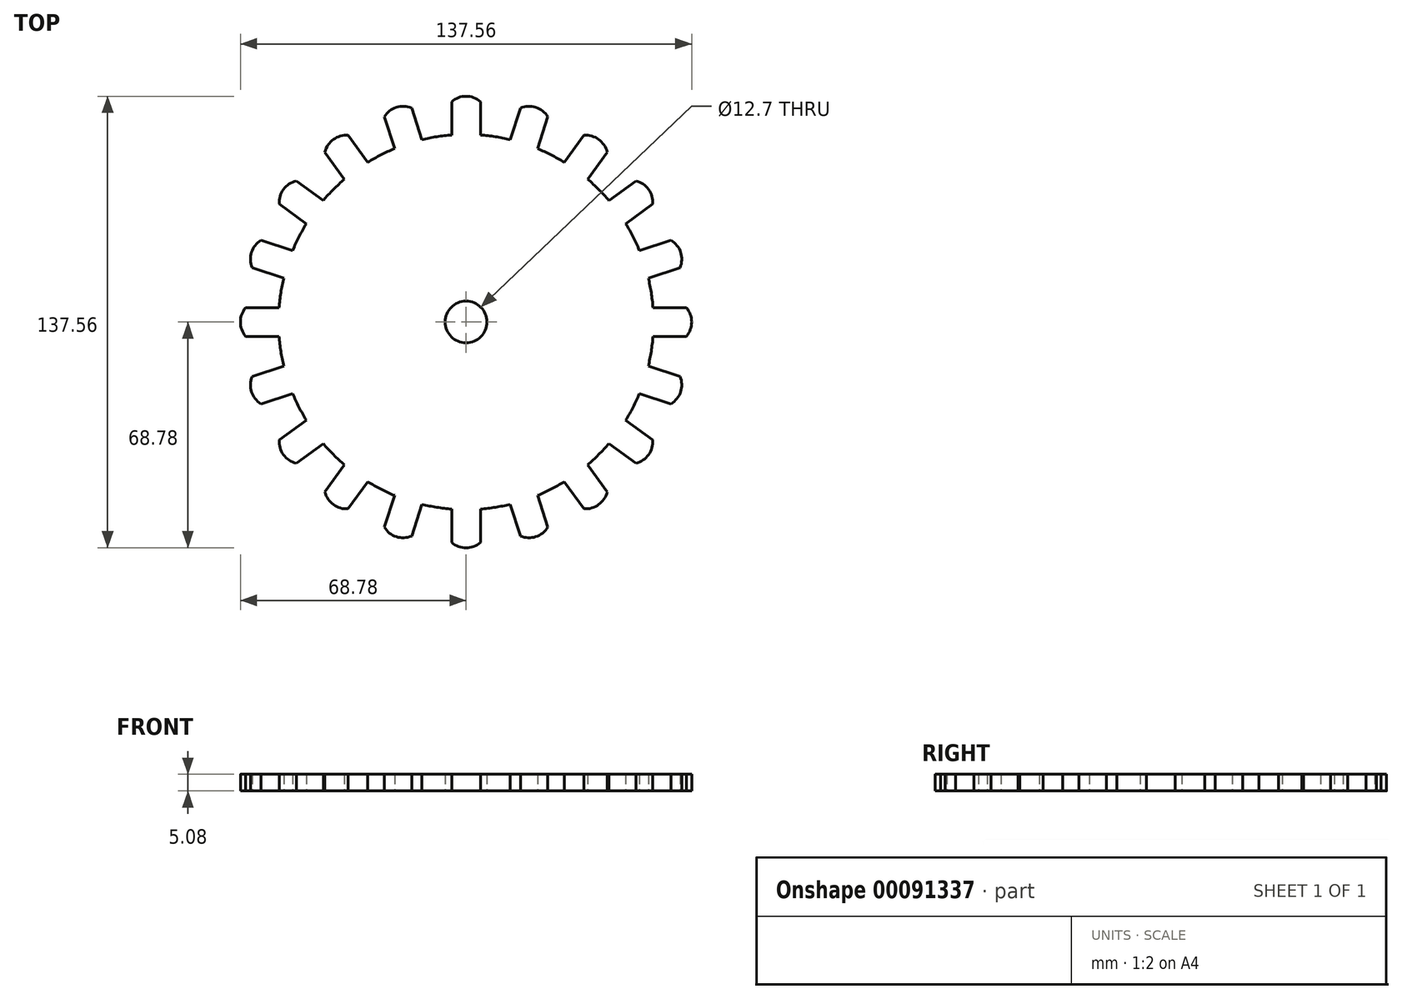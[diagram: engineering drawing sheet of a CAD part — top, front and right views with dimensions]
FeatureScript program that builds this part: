
annotation { "Feature Type Name" : "Feature", "Feature Type Description" : "" }
export const myFeature = defineFeature(function(context is Context, id is Id, definition is map)
    precondition{}
    {
        {
            var Q0;
            Q0=qCreatedBy(makeId("Top.planeOp"),FACE);
            var sketch = newSketch(context, id + "F0", { "sketchPlane" : qUnion([Q0])});
            skArc(sketch, "E0", {"start": v(-4.4, 56.98) * mm, "mid": v(-8.94, 56.45) * mm, "end": v(-13.43, 55.55) * mm});
            skLineSegment(sketch, "E1.left", {"start": v(4.4, 56.98) * mm, "end": v(4.4, 67.14) * mm});
            skLineSegment(sketch, "E1.right", {"start": v(-4.4, 56.98) * mm, "end": v(-4.4, 67.14) * mm});
            skArc(sketch, "E2", {"start": v(4.4, 67.14) * mm, "mid": v(0, 68.78) * mm, "end": v(-4.4, 67.14) * mm});
            skPoint(sketch, "E3.start.orphan", {"position": v(0, 67.14) * mm});
            skLineSegment(sketch, "E4.1.0", {"start": v(-13.43, 55.55) * mm, "end": v(-16.57, 65.21) * mm});
            skArc(sketch, "E4.1.1", {"start": v(-16.57, 65.21) * mm, "mid": v(-21.25, 65.41) * mm, "end": v(-24.92, 62.5) * mm});
            skLineSegment(sketch, "E4.1.2", {"start": v(-21.79, 52.83) * mm, "end": v(-24.92, 62.5) * mm});
            skLineSegment(sketch, "E4.2.0", {"start": v(-29.94, 48.68) * mm, "end": v(-35.91, 56.9) * mm});
            skArc(sketch, "E4.2.1", {"start": v(-35.91, 56.9) * mm, "mid": v(-40.43, 55.64) * mm, "end": v(-43.02, 51.74) * mm});
            skLineSegment(sketch, "E4.2.2", {"start": v(-37.05, 43.52) * mm, "end": v(-43.02, 51.74) * mm});
            skLineSegment(sketch, "E4.3.0", {"start": v(-43.52, 37.05) * mm, "end": v(-51.74, 43.02) * mm});
            skArc(sketch, "E4.3.1", {"start": v(-51.74, 43.02) * mm, "mid": v(-55.64, 40.43) * mm, "end": v(-56.9, 35.91) * mm});
            skLineSegment(sketch, "E4.3.2", {"start": v(-48.68, 29.94) * mm, "end": v(-56.9, 35.91) * mm});
            skLineSegment(sketch, "E4.4.0", {"start": v(-52.83, 21.79) * mm, "end": v(-62.5, 24.92) * mm});
            skArc(sketch, "E4.4.1", {"start": v(-62.5, 24.92) * mm, "mid": v(-65.41, 21.25) * mm, "end": v(-65.21, 16.57) * mm});
            skLineSegment(sketch, "E4.4.2", {"start": v(-55.55, 13.43) * mm, "end": v(-65.21, 16.57) * mm});
            skLineSegment(sketch, "E4.5.0", {"start": v(-56.98, 4.4) * mm, "end": v(-67.14, 4.4) * mm});
            skArc(sketch, "E4.5.1", {"start": v(-67.14, 4.4) * mm, "mid": v(-68.78, 0) * mm, "end": v(-67.14, -4.4) * mm});
            skLineSegment(sketch, "E4.5.2", {"start": v(-56.98, -4.4) * mm, "end": v(-67.14, -4.4) * mm});
            skLineSegment(sketch, "E4.6.0", {"start": v(-55.55, -13.43) * mm, "end": v(-65.21, -16.57) * mm});
            skArc(sketch, "E4.6.1", {"start": v(-65.21, -16.57) * mm, "mid": v(-65.41, -21.25) * mm, "end": v(-62.5, -24.92) * mm});
            skLineSegment(sketch, "E4.6.2", {"start": v(-52.83, -21.79) * mm, "end": v(-62.5, -24.92) * mm});
            skLineSegment(sketch, "E4.7.0", {"start": v(-48.68, -29.94) * mm, "end": v(-56.9, -35.91) * mm});
            skArc(sketch, "E4.7.1", {"start": v(-56.9, -35.91) * mm, "mid": v(-55.64, -40.43) * mm, "end": v(-51.74, -43.02) * mm});
            skLineSegment(sketch, "E4.7.2", {"start": v(-43.52, -37.05) * mm, "end": v(-51.74, -43.02) * mm});
            skLineSegment(sketch, "E4.8.0", {"start": v(-37.05, -43.52) * mm, "end": v(-43.02, -51.74) * mm});
            skArc(sketch, "E4.8.1", {"start": v(-43.02, -51.74) * mm, "mid": v(-40.43, -55.64) * mm, "end": v(-35.91, -56.9) * mm});
            skLineSegment(sketch, "E4.8.2", {"start": v(-29.94, -48.68) * mm, "end": v(-35.91, -56.9) * mm});
            skLineSegment(sketch, "E4.9.0", {"start": v(-21.79, -52.83) * mm, "end": v(-24.92, -62.5) * mm});
            skArc(sketch, "E4.9.1", {"start": v(-24.92, -62.5) * mm, "mid": v(-21.25, -65.41) * mm, "end": v(-16.57, -65.21) * mm});
            skLineSegment(sketch, "E4.9.2", {"start": v(-13.43, -55.55) * mm, "end": v(-16.57, -65.21) * mm});
            skLineSegment(sketch, "E4.10.0", {"start": v(-4.4, -56.98) * mm, "end": v(-4.4, -67.14) * mm});
            skArc(sketch, "E4.10.1", {"start": v(-4.4, -67.14) * mm, "mid": v(0, -68.78) * mm, "end": v(4.4, -67.14) * mm});
            skLineSegment(sketch, "E4.10.2", {"start": v(4.4, -56.98) * mm, "end": v(4.4, -67.14) * mm});
            skLineSegment(sketch, "E4.11.0", {"start": v(13.43, -55.55) * mm, "end": v(16.57, -65.21) * mm});
            skArc(sketch, "E4.11.1", {"start": v(16.57, -65.21) * mm, "mid": v(21.25, -65.41) * mm, "end": v(24.92, -62.5) * mm});
            skLineSegment(sketch, "E4.11.2", {"start": v(21.79, -52.83) * mm, "end": v(24.92, -62.5) * mm});
            skLineSegment(sketch, "E4.12.0", {"start": v(29.94, -48.68) * mm, "end": v(35.91, -56.9) * mm});
            skArc(sketch, "E4.12.1", {"start": v(35.91, -56.9) * mm, "mid": v(40.43, -55.64) * mm, "end": v(43.02, -51.74) * mm});
            skLineSegment(sketch, "E4.12.2", {"start": v(37.05, -43.52) * mm, "end": v(43.02, -51.74) * mm});
            skLineSegment(sketch, "E4.13.0", {"start": v(43.52, -37.05) * mm, "end": v(51.74, -43.02) * mm});
            skArc(sketch, "E4.13.1", {"start": v(51.74, -43.02) * mm, "mid": v(55.64, -40.43) * mm, "end": v(56.9, -35.91) * mm});
            skLineSegment(sketch, "E4.13.2", {"start": v(48.68, -29.94) * mm, "end": v(56.9, -35.91) * mm});
            skLineSegment(sketch, "E4.14.0", {"start": v(52.83, -21.79) * mm, "end": v(62.5, -24.92) * mm});
            skArc(sketch, "E4.14.1", {"start": v(62.5, -24.92) * mm, "mid": v(65.41, -21.25) * mm, "end": v(65.21, -16.57) * mm});
            skLineSegment(sketch, "E4.14.2", {"start": v(55.55, -13.43) * mm, "end": v(65.21, -16.57) * mm});
            skLineSegment(sketch, "E4.15.0", {"start": v(56.98, -4.4) * mm, "end": v(67.14, -4.4) * mm});
            skArc(sketch, "E4.15.1", {"start": v(67.14, -4.4) * mm, "mid": v(68.78, 0) * mm, "end": v(67.14, 4.4) * mm});
            skLineSegment(sketch, "E4.15.2", {"start": v(56.98, 4.4) * mm, "end": v(67.14, 4.4) * mm});
            skLineSegment(sketch, "E4.16.0", {"start": v(55.55, 13.43) * mm, "end": v(65.21, 16.57) * mm});
            skArc(sketch, "E4.16.1", {"start": v(65.21, 16.57) * mm, "mid": v(65.41, 21.25) * mm, "end": v(62.5, 24.92) * mm});
            skLineSegment(sketch, "E4.16.2", {"start": v(52.83, 21.79) * mm, "end": v(62.5, 24.92) * mm});
            skLineSegment(sketch, "E4.17.0", {"start": v(48.68, 29.94) * mm, "end": v(56.9, 35.91) * mm});
            skArc(sketch, "E4.17.1", {"start": v(56.9, 35.91) * mm, "mid": v(55.64, 40.43) * mm, "end": v(51.74, 43.02) * mm});
            skLineSegment(sketch, "E4.17.2", {"start": v(43.52, 37.05) * mm, "end": v(51.74, 43.02) * mm});
            skLineSegment(sketch, "E4.18.0", {"start": v(37.05, 43.52) * mm, "end": v(43.02, 51.74) * mm});
            skArc(sketch, "E4.18.1", {"start": v(43.02, 51.74) * mm, "mid": v(40.43, 55.64) * mm, "end": v(35.91, 56.9) * mm});
            skLineSegment(sketch, "E4.18.2", {"start": v(29.94, 48.68) * mm, "end": v(35.91, 56.9) * mm});
            skLineSegment(sketch, "E4.19.0", {"start": v(21.79, 52.83) * mm, "end": v(24.92, 62.5) * mm});
            skArc(sketch, "E4.19.1", {"start": v(24.92, 62.5) * mm, "mid": v(21.25, 65.41) * mm, "end": v(16.57, 65.21) * mm});
            skLineSegment(sketch, "E4.19.2", {"start": v(13.43, 55.55) * mm, "end": v(16.57, 65.21) * mm});
            skArc(sketch, "E5.trimOffspring", {"start": v(-21.79, 52.83) * mm, "mid": v(-25.95, 50.92) * mm, "end": v(-29.94, 48.68) * mm});
            skArc(sketch, "E6.trimOffspring", {"start": v(-37.05, 43.52) * mm, "mid": v(-40.41, 40.41) * mm, "end": v(-43.52, 37.05) * mm});
            skArc(sketch, "E7.trimOffspring", {"start": v(-48.68, 29.94) * mm, "mid": v(-50.92, 25.95) * mm, "end": v(-52.83, 21.79) * mm});
            skArc(sketch, "E8.trimOffspring", {"start": v(-55.55, 13.43) * mm, "mid": v(-56.45, 8.94) * mm, "end": v(-56.98, 4.4) * mm});
            skArc(sketch, "E9.trimOffspring", {"start": v(-56.98, -4.4) * mm, "mid": v(-56.45, -8.94) * mm, "end": v(-55.55, -13.43) * mm});
            skArc(sketch, "E10.trimOffspring", {"start": v(-52.83, -21.79) * mm, "mid": v(-50.92, -25.95) * mm, "end": v(-48.68, -29.94) * mm});
            skArc(sketch, "E11.trimOffspring", {"start": v(-43.52, -37.05) * mm, "mid": v(-40.41, -40.41) * mm, "end": v(-37.05, -43.52) * mm});
            skArc(sketch, "E12.trimOffspring", {"start": v(-29.94, -48.68) * mm, "mid": v(-25.95, -50.92) * mm, "end": v(-21.79, -52.83) * mm});
            skArc(sketch, "E13.trimOffspring", {"start": v(-13.43, -55.55) * mm, "mid": v(-8.94, -56.45) * mm, "end": v(-4.4, -56.98) * mm});
            skArc(sketch, "E14.trimOffspring", {"start": v(4.4, -56.98) * mm, "mid": v(8.94, -56.45) * mm, "end": v(13.43, -55.55) * mm});
            skArc(sketch, "E15.trimOffspring", {"start": v(21.79, -52.83) * mm, "mid": v(25.95, -50.92) * mm, "end": v(29.94, -48.68) * mm});
            skArc(sketch, "E16.trimOffspring", {"start": v(37.05, -43.52) * mm, "mid": v(40.41, -40.41) * mm, "end": v(43.52, -37.05) * mm});
            skArc(sketch, "E17.trimOffspring", {"start": v(48.68, -29.94) * mm, "mid": v(50.92, -25.95) * mm, "end": v(52.83, -21.79) * mm});
            skArc(sketch, "E18.trimOffspring", {"start": v(55.55, -13.43) * mm, "mid": v(56.45, -8.94) * mm, "end": v(56.98, -4.4) * mm});
            skArc(sketch, "E19.trimOffspring", {"start": v(56.98, 4.4) * mm, "mid": v(56.45, 8.94) * mm, "end": v(55.55, 13.43) * mm});
            skArc(sketch, "E20.trimOffspring", {"start": v(52.83, 21.79) * mm, "mid": v(50.92, 25.95) * mm, "end": v(48.68, 29.94) * mm});
            skArc(sketch, "E21.trimOffspring", {"start": v(43.52, 37.05) * mm, "mid": v(40.41, 40.41) * mm, "end": v(37.05, 43.52) * mm});
            skArc(sketch, "E22.trimOffspring", {"start": v(29.94, 48.68) * mm, "mid": v(25.95, 50.92) * mm, "end": v(21.79, 52.83) * mm});
            skArc(sketch, "E23.trimOffspring", {"start": v(13.43, 55.55) * mm, "mid": v(8.94, 56.45) * mm, "end": v(4.4, 56.98) * mm});
            skCircle(sketch, "E24", {"center": v(0, 0) * mm, "radius": 6.35 * mm});
            skSolve(sketch);
        }
        {
            var Q0;
            Q0=makeQuery(id+"F0.imprint","IMPRINT",FACE,{"disambiguationData":[TD([[makeQuery(id+"F0.imprint","IMPRINT",EDGE,{"derivedFrom":sQuery(id+"F0.wireOp",EDGE,"E0")}),1.0]])]});
            extrude(context, id + "F1", {"entities" : qUnion([Q0]), "depth" : 5.08 * mm});
        }
    });
